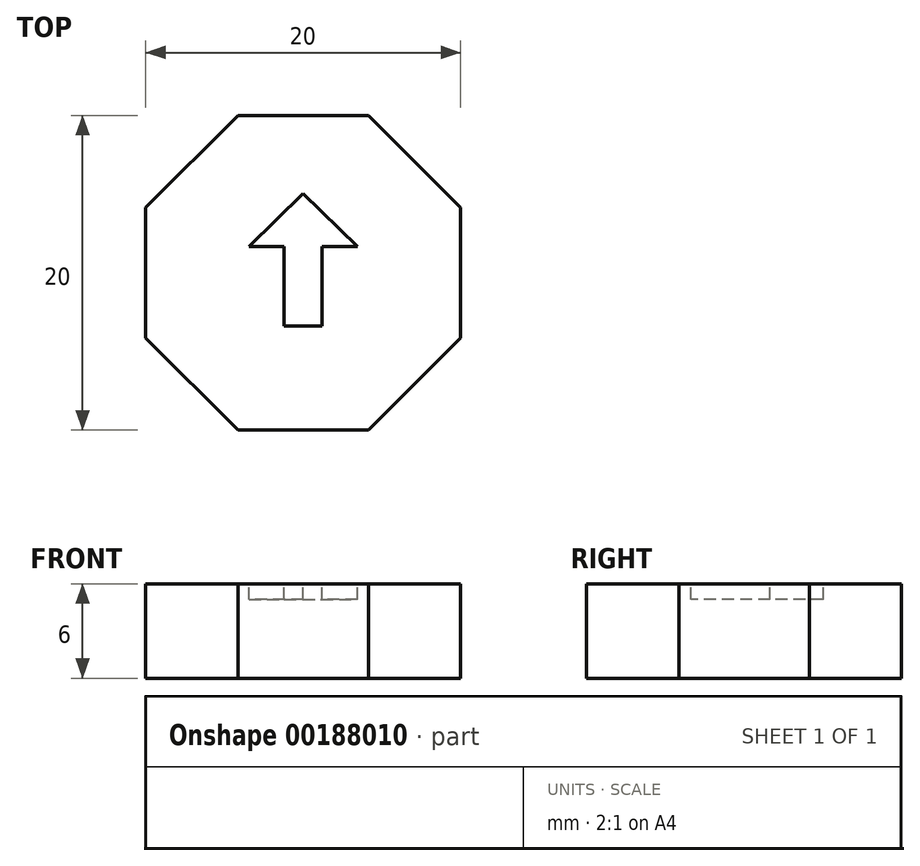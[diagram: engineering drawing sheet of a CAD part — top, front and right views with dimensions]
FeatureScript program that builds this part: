
annotation { "Feature Type Name" : "Feature", "Feature Type Description" : "" }
export const myFeature = defineFeature(function(context is Context, id is Id, definition is map)
    precondition{}
    {
        {
            var Q0;
            Q0=qCreatedBy(makeId("Top.planeOp"),FACE);
            var sketch = newSketch(context, id + "F0", { "sketchPlane" : qUnion([Q0])});
            skCircle(sketch, "E0.cCircle", {"center": v(0, 0) * mm, "radius": 10 * mm, "construction": true});
            skLineSegment(sketch, "E0.0", {"start": v(10, 4.14) * mm, "end": v(10, -4.14) * mm});
            skLineSegment(sketch, "E0.1", {"start": v(10, -4.14) * mm, "end": v(4.14, -10) * mm});
            skLineSegment(sketch, "E0.2", {"start": v(4.14, -10) * mm, "end": v(-4.14, -10) * mm});
            skLineSegment(sketch, "E0.3", {"start": v(-4.14, -10) * mm, "end": v(-10, -4.14) * mm});
            skLineSegment(sketch, "E0.4", {"start": v(-10, -4.14) * mm, "end": v(-10, 4.14) * mm});
            skLineSegment(sketch, "E0.5", {"start": v(-10, 4.14) * mm, "end": v(-4.14, 10) * mm});
            skLineSegment(sketch, "E0.6", {"start": v(-4.14, 10) * mm, "end": v(4.14, 10) * mm});
            skLineSegment(sketch, "E0.7", {"start": v(4.14, 10) * mm, "end": v(10, 4.14) * mm});
            skPoint(sketch, "E0.0.midPoint", {"position": v(10, 0) * mm});
            skSolve(sketch);
        }
        {
            var Q0;
            Q0 = qSketchRegion(id + "F0", true);
            extrude(context, id + "F1", {"entities" : qUnion([Q0]), "depth" : 6 * mm});
        }
        {
            var Q0;
            Q0=makeQuery(id+"F1.opExtrude","CAP_FACE",FACE,{"disambiguationData":[OSD([sQuery(id+"F0.wireOp",EDGE,"E0.0"),sQuery(id+"F0.wireOp",EDGE,"E0.1"),sQuery(id+"F0.wireOp",EDGE,"E0.2"),sQuery(id+"F0.wireOp",EDGE,"E0.3"),sQuery(id+"F0.wireOp",EDGE,"E0.4"),sQuery(id+"F0.wireOp",EDGE,"E0.5"),sQuery(id+"F0.wireOp",EDGE,"E0.6"),sQuery(id+"F0.wireOp",EDGE,"E0.7")])],"isStart":false});
            var sketch = newSketch(context, id + "F2", { "sketchPlane" : qUnion([Q0])});
            skLineSegment(sketch, "E1", {"start": v(0, 5.05) * mm, "end": v(-3.44, 1.66) * mm});
            skLineSegment(sketch, "E2", {"start": v(-3.44, 1.66) * mm, "end": v(-1.2, 1.66) * mm});
            skLineSegment(sketch, "E3", {"start": v(-1.2, 1.66) * mm, "end": v(-1.2, -3.38) * mm});
            skLineSegment(sketch, "E4", {"start": v(-1.2, -3.38) * mm, "end": v(0, -3.38) * mm});
            skLineSegment(sketch, "E5.MirrorCS", {"start": v(0, 5.05) * mm, "end": v(3.44, 1.66) * mm});
            skLineSegment(sketch, "E6.MirrorCS", {"start": v(3.44, 1.66) * mm, "end": v(1.2, 1.66) * mm});
            skLineSegment(sketch, "E7.MirrorCS", {"start": v(1.2, 1.66) * mm, "end": v(1.2, -3.38) * mm});
            skLineSegment(sketch, "E8.MirrorCS", {"start": v(1.2, -3.38) * mm, "end": v(0, -3.38) * mm});
            skSolve(sketch);
        }
        {
            var Q0;
            Q0 = qSketchRegion(id + "F2", true);
            extrude(context, id + "F3", {"entities" : qUnion([Q0]), "operationType" : NewBodyOperationType.REMOVE, "oppositeDirection" : true, "depth" : 1 * mm});
        }
    });
